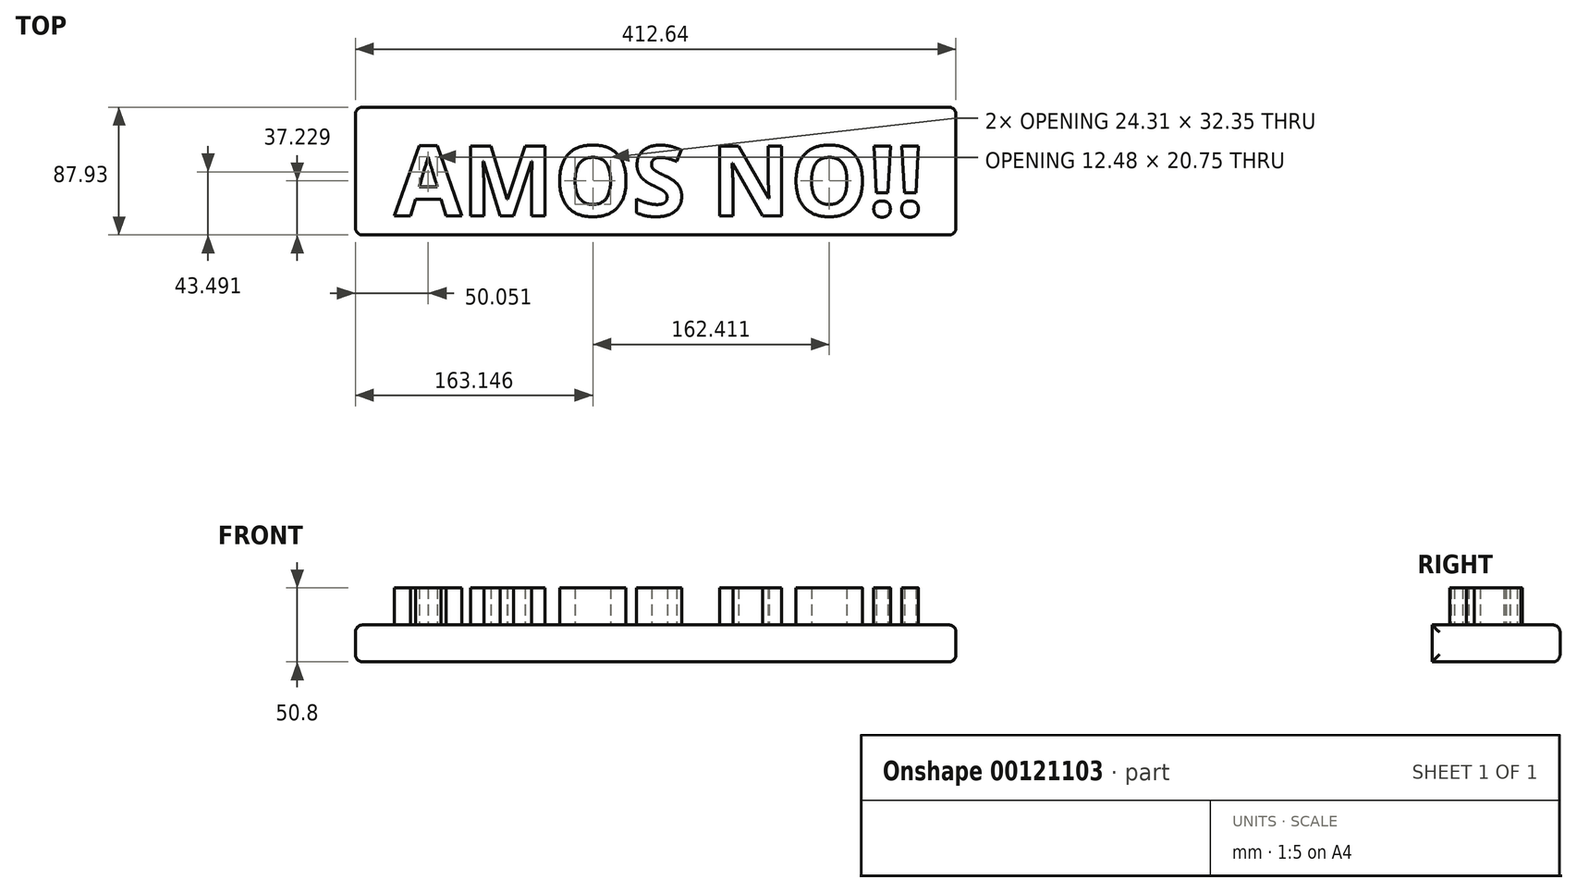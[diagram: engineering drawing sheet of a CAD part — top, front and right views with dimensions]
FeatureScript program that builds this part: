
annotation { "Feature Type Name" : "Feature", "Feature Type Description" : "" }
export const myFeature = defineFeature(function(context is Context, id is Id, definition is map)
    precondition{}
    {
        {
            var Q0;
            Q0=qCreatedBy(makeId("Top.planeOp"),FACE);
            var sketch = newSketch(context, id + "F0", { "sketchPlane" : qUnion([Q0])});
            skLineSegment(sketch, "E0.bottom", {"start": v(-210.97, 35.62) * mm, "end": v(190.68, 35.62) * mm});
            skLineSegment(sketch, "E0.top", {"start": v(-210.97, -76.46) * mm, "end": v(190.68, -76.46) * mm});
            skLineSegment(sketch, "E0.left", {"start": v(-210.97, 35.62) * mm, "end": v(-210.97, -76.46) * mm});
            skLineSegment(sketch, "E0.right", {"start": v(190.68, 35.62) * mm, "end": v(190.68, -76.46) * mm});
            skText(sketch, "E1", { "text": "AMOS NO!!\n", "fontName": "OpenSans-Bold.ttf"});
            const initialGuessF0  = {"E1": [-0.1939, -0.04833, 1, 0, 0.04833]};
            skSetInitialGuess(sketch, initialGuessF0);
            skSolve(sketch);
        }
        {
            var Q0;
            Q0=makeQuery(id+"F0.imprint","IMPRINT",FACE,{"disambiguationData":[TD([[makeQuery(id+"F0.imprint","IMPRINT",EDGE,{"derivedFrom":sQuery(id+"F0.wireOp",EDGE,"E1.sketch_text.stroke-0")}),-1.0]])]});
            var Q1;
            Q1=makeQuery(id+"F0.imprint","IMPRINT",FACE,{"disambiguationData":[TD([[makeQuery(id+"F0.imprint","IMPRINT",EDGE,{"derivedFrom":sQuery(id+"F0.wireOp",EDGE,"E1.sketch_text.stroke-12")}),-1.0]])]});
            var Q2;
            Q2=makeQuery(id+"F0.imprint","IMPRINT",FACE,{"disambiguationData":[TD([[makeQuery(id+"F0.imprint","IMPRINT",EDGE,{"derivedFrom":sQuery(id+"F0.wireOp",EDGE,"E1.sketch_text.stroke-31")}),-1.0]])]});
            var Q3;
            Q3=makeQuery(id+"F0.imprint","IMPRINT",FACE,{"disambiguationData":[TD([[makeQuery(id+"F0.imprint","IMPRINT",EDGE,{"derivedFrom":sQuery(id+"F0.wireOp",EDGE,"E1.sketch_text.stroke-45")}),-1.0]])]});
            var Q4;
            Q4=makeQuery(id+"F0.imprint","IMPRINT",FACE,{"disambiguationData":[TD([[makeQuery(id+"F0.imprint","IMPRINT",EDGE,{"derivedFrom":sQuery(id+"F0.wireOp",EDGE,"E1.sketch_text.stroke-87")}),-1.0]])]});
            var Q5;
            Q5=makeQuery(id+"F0.imprint","IMPRINT",FACE,{"disambiguationData":[TD([[makeQuery(id+"F0.imprint","IMPRINT",EDGE,{"derivedFrom":sQuery(id+"F0.wireOp",EDGE,"E1.sketch_text.stroke-73")}),-1.0]])]});
            var Q6;
            Q6=makeQuery(id+"F0.imprint","IMPRINT",FACE,{"disambiguationData":[TD([[makeQuery(id+"F0.imprint","IMPRINT",EDGE,{"derivedFrom":sQuery(id+"F0.wireOp",EDGE,"E1.sketch_text.stroke-101")}),-1.0]])]});
            var Q7;
            Q7=makeQuery(id+"F0.imprint","IMPRINT",FACE,{"disambiguationData":[TD([[makeQuery(id+"F0.imprint","IMPRINT",EDGE,{"derivedFrom":sQuery(id+"F0.wireOp",EDGE,"E1.sketch_text.stroke-105")}),-1.0]])]});
            var Q8;
            Q8=makeQuery(id+"F0.imprint","IMPRINT",FACE,{"disambiguationData":[TD([[makeQuery(id+"F0.imprint","IMPRINT",EDGE,{"derivedFrom":sQuery(id+"F0.wireOp",EDGE,"E1.sketch_text.stroke-113")}),-1.0]])]});
            var Q9;
            Q9=makeQuery(id+"F0.imprint","IMPRINT",FACE,{"disambiguationData":[TD([[makeQuery(id+"F0.imprint","IMPRINT",EDGE,{"derivedFrom":sQuery(id+"F0.wireOp",EDGE,"E1.sketch_text.stroke-117")}),-1.0]])]});
            extrude(context, id + "F1", {"entities" : qUnion([Q0, Q1, Q2, Q3, Q4, Q5, Q6, Q7, Q8, Q9]), "depth" : 25.4 * mm});
        }
        {
            var Q0;
            Q0=makeQuery(id+"F1.opExtrude","CAP_FACE",FACE,{"disambiguationData":[OSD([sQuery(id+"F0.wireOp",EDGE,"E1.sketch_text.stroke-31"),sQuery(id+"F0.wireOp",EDGE,"E1.sketch_text.stroke-32"),sQuery(id+"F0.wireOp",EDGE,"E1.sketch_text.stroke-33"),sQuery(id+"F0.wireOp",EDGE,"E1.sketch_text.stroke-34"),sQuery(id+"F0.wireOp",EDGE,"E1.sketch_text.stroke-35"),sQuery(id+"F0.wireOp",EDGE,"E1.sketch_text.stroke-36"),sQuery(id+"F0.wireOp",EDGE,"E1.sketch_text.stroke-37"),sQuery(id+"F0.wireOp",EDGE,"E1.sketch_text.stroke-38"),sQuery(id+"F0.wireOp",EDGE,"E1.sketch_text.stroke-39"),sQuery(id+"F0.wireOp",EDGE,"E1.sketch_text.stroke-40"),sQuery(id+"F0.wireOp",EDGE,"E1.sketch_text.stroke-41"),sQuery(id+"F0.wireOp",EDGE,"E1.sketch_text.stroke-42"),sQuery(id+"F0.wireOp",EDGE,"E1.sketch_text.stroke-43"),sQuery(id+"F0.wireOp",EDGE,"E1.sketch_text.stroke-44")])],"isStart":true});
            var sketch = newSketch(context, id + "F2", { "sketchPlane" : qUnion([Q0])});
            skLineSegment(sketch, "E2.bottom", {"start": v(-220.73, 61.52) * mm, "end": v(191.9, 61.52) * mm});
            skLineSegment(sketch, "E2.top", {"start": v(-220.73, -26.41) * mm, "end": v(191.9, -26.41) * mm});
            skLineSegment(sketch, "E2.left", {"start": v(-220.73, 61.52) * mm, "end": v(-220.73, -26.41) * mm});
            skLineSegment(sketch, "E2.right", {"start": v(191.9, 61.52) * mm, "end": v(191.9, -26.41) * mm});
            skSolve(sketch);
        }
        {
            var Q0;
            Q0=makeQuery(id+"F2.imprint","IMPRINT",FACE,{"disambiguationData":[TD([[makeQuery(id+"F2.imprint","IMPRINT",EDGE,{"derivedFrom":sQuery(id+"F2.wireOp",EDGE,"E2.bottom")}),-1.0]])]});
            var Q1;
            Q1=makeQuery(id+"F2.imprint","IMPRINT",FACE,{"disambiguationData":[TD([[makeQuery(id+"F2.imprint","IMPRINT",EDGE,{"derivedFrom":makeQuery(id+"F1.opExtrude","CAP_EDGE",EDGE,{"disambiguationData":[OSD([sQuery(id+"F0.wireOp",EDGE,"E1.sketch_text.stroke-31")])],"isStart":true})}),1.0]])]});
            var Q2;
            Q2=makeQuery(id+"F2.imprint","IMPRINT",FACE,{"disambiguationData":[TD([[makeQuery(id+"F2.imprint","IMPRINT",EDGE,{"derivedFrom":makeQuery(id+"F1.opExtrude","CAP_EDGE",EDGE,{"disambiguationData":[OSD([sQuery(id+"F0.wireOp",EDGE,"E1.sketch_text.stroke-39")])],"isStart":true})}),-1.0]])]});
            extrude(context, id + "F3", {"entities" : qUnion([Q0, Q1, Q2]), "depth" : 25.4 * mm});
        }
        {
            var Q0;
            Q0=makeQuery(id+"F3.opExtrude","SWEPT_FACE",FACE,{"disambiguationData":[OSD([sQuery(id+"F2.wireOp",EDGE,"E2.left")])]});
            var Q1;
            Q1=makeQuery(id+"F3.opExtrude","SWEPT_FACE",FACE,{"disambiguationData":[OSD([sQuery(id+"F2.wireOp",EDGE,"E2.top")])]});
            fillet(context, id + "F4", {"entities" : qUnion([Q0, Q1]), "radius" : 5.08 * mm, "tangentPropagation" : true, "allowEdgeOverflow" : false});
        }
        {
            var Q0;
            Q0=makeQuery(id+"F3.opExtrude","SWEPT_FACE",FACE,{"disambiguationData":[OSD([sQuery(id+"F2.wireOp",EDGE,"E2.right")])]});
            var Q1;
            {var subQ0=sQuery(id+"F2.wireOp",EDGE,"E2.right");Q1=makeQuery(id+"F4.opFillet","BLEND_EDGE",EDGE,{"blendedFrom":[makeQuery(id+"F3.opExtrude","SWEPT_EDGE",EDGE,{"disambiguationData":[OSD([sQuery(id+"F2.wireOp",EDGE,"E2.top"),subQ0])]}),makeQuery(id+"F3.opExtrude","SWEPT_FACE",FACE,{"disambiguationData":[OSD([subQ0])]})],"blendedInto":[makeQuery(id+"F3.opExtrude","SWEPT_FACE",FACE,{"disambiguationData":[OSD([subQ0])]})]});}
            var Q2;
            {var subQ0=sQuery(id+"F2.wireOp",EDGE,"E2.top");Q2=makeQuery(id+"F4.opFillet","BLEND_EDGE",EDGE,{"blendedFrom":[makeQuery(id+"F3.opExtrude","SWEPT_EDGE",EDGE,{"disambiguationData":[OSD([subQ0,sQuery(id+"F2.wireOp",EDGE,"E2.right")])]}),makeQuery(id+"F3.opExtrude","SWEPT_FACE",FACE,{"disambiguationData":[OSD([subQ0])]})],"blendedInto":[makeQuery(id+"F3.opExtrude","SWEPT_FACE",FACE,{"disambiguationData":[OSD([subQ0])]})]});}
            var Q3;
            Q3=makeQuery(id+"F4.opFillet","BLEND_FACE",FACE,{"disambiguationData":[OSD([sQuery(id+"F2.wireOp",EDGE,"E2.top"),sQuery(id+"F2.wireOp",EDGE,"E2.right")])]});
            fillet(context, id + "F5", {"entities" : qUnion([Q0, Q1, Q2, Q3]), "radius" : 5.08 * mm, "tangentPropagation" : true, "allowEdgeOverflow" : false});
        }
    });
